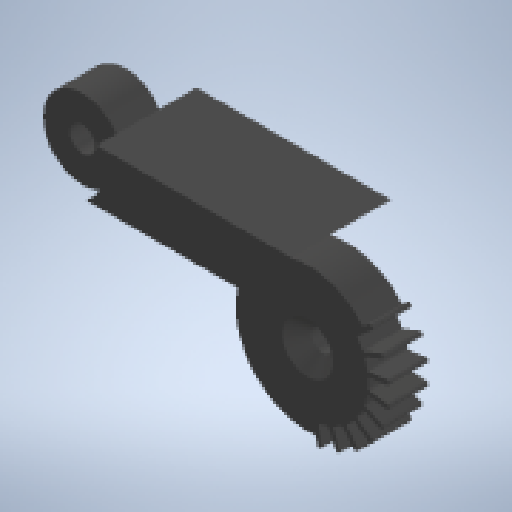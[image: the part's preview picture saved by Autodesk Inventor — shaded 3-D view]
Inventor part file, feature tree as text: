
AUTODESK INVENTOR PART (.ipt)
format: ipt  version: 2025.2 (Build 292293000, 293)  size: 325,632 bytes
history: native  units: mm
features: sketch x7, extrude x5, fillet x4, hole x2, other x1
ambient origin geometry x8: Origin, YZ Plane, XZ Plane, XY Plane, X Axis, Y Axis, Z Axis, Center Point
bodies: Body1 (feature_tree)
feature tree (19):
  other  "Sólido1"
  sketch  "Esboço1"  dims[d0=11.0mm d1=20.0mm]
  extrude  "Extrusão1"  Depth=20.0mm
  extrude  "Extrusão2"  Depth=6.8mm
  extrude  "Extrusão3"  Depth=21.0mm
  extrude  "Extrusão4"  Depth=6.0mm TaperAngle=0.0deg
  hole  "Furo1"  [1 undecoded]
  hole  "Furo2"  [1 undecoded]
  fillet  "Arredondamento1"  Radius=1.3mm
  fillet  "Arredondamento2"  Radius=0.65mm
  fillet  "Arredondamento3"  [1 undecoded]
  fillet  "Arredondamento4"  [1 undecoded]
  extrude  "Extrusão5"  TaperAngle=90.0deg  [1 undecoded]
  sketch  "Esboço2"  dims[d2=34.0mm d3=6.8mm]
  sketch  "Esboço - Padrão circular2"  dims[d4=27.0mm d8=21.0mm]
  sketch  "Esboço - Padrão circular3"  dims[d9=5.45mm d10=0.0mm d11=6.0mm d12=0.0mm]
  sketch  "Esboço3"  dims[d13=5.45mm d14=0.0mm d15=8.45mm d16=0.0mm]
  sketch  "Esboço4"  dims[d17=16.8mm d18=8.726646mm d24=1.3mm d25=0.65mm d26=90.0deg d29=90.0deg]
  sketch  "Esboço5"  dims[d35=2.740167mm d36=90.0deg d37=90.0deg d38=70.0mm d40=90.0deg d42=20.0mm d44=120.0deg d46=90.0deg d47=180.0deg d48=3.0mm d49=6.0mm d50=7.0mm d51=2.0mm d52=90.0deg d53=8.0mm d54=20.594885mm d55=5.5mm d56=20.0mm d57=3.5mm d58=6.0mm d59=7.0mm d60=2.0mm d61=90.0deg d62=8.0mm d63=20.594885mm d64=0.25mm d65=0.25mm d66=0.25mm d67=0.25mm d69=4.3mm d70=3.5mm d71=1.3mm d72=0.0mm d19=0.5mm d20=0.872665mm]
note: 5 required parameter values undecoded (feature->parameter linkage not recoverable at this tier; creation-order binding heuristic only, values carry confidence <= 0.55)
